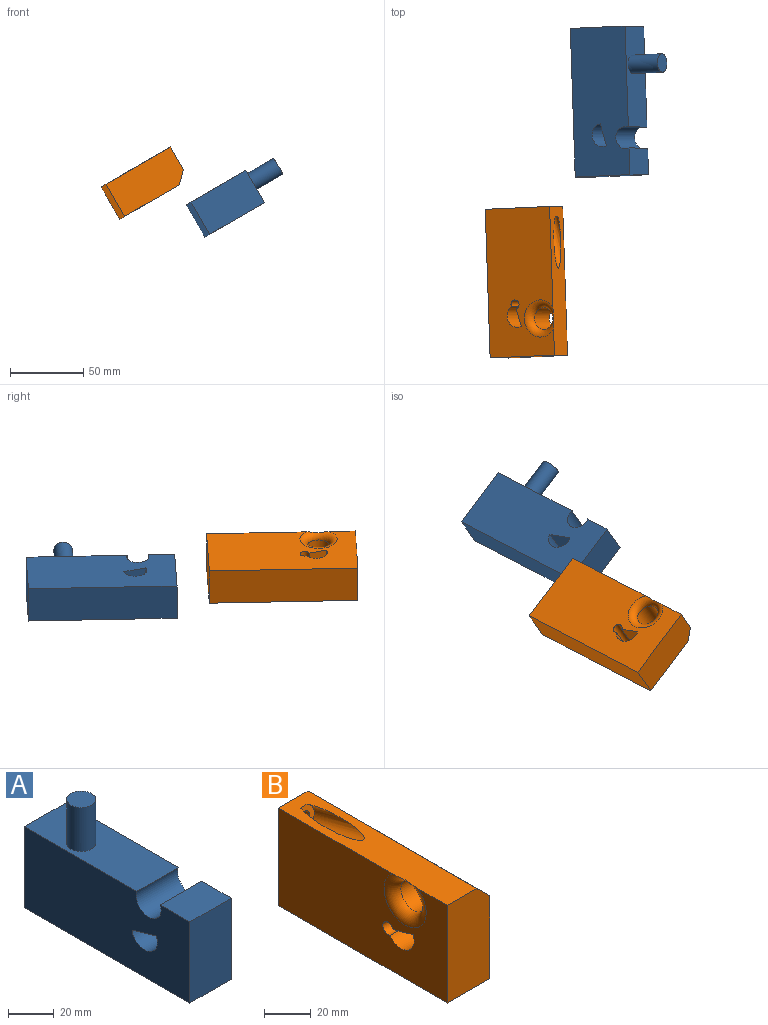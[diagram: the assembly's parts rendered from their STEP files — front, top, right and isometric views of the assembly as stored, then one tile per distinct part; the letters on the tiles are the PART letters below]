
ASSEMBLY  parts=2 mates=1
PART A: 12 faces, bbox 25.4x101.6x66.5 mm
  f0: plane 43.18x25.4mm, normal (0,1,0), area 1096.8mm2, adj f1,f7,f8,f9
  f1: plane 69.02x25.4mm, normal (0,0,1), area 1628.4mm2, adj f0,f2,f8,f9,f10
  f2: cylinder r=7.62mm len=25.4mm, axis (-1,0,0), area 739.6mm2, adj f1,f3,f8,f9
  f3: plane 25.4x18.22mm, normal (0,0,1), area 462.7mm2, adj f2,f4,f8,f9
  f4: plane 43.18x25.4mm, normal (0,-1,0), area 1096.8mm2, adj f3,f7,f8,f9
  f5: cylinder r=7.88mm len=25.4mm, axis (-1,0,0), area 675.4mm2, adj f6,f8,f9
  f6: plane 25.4x15.03mm, normal (0,-0.28,-0.96), area 397.8mm2, adj f5,f8,f9
  f7: plane 101.6x25.4mm, normal (0,0,-1), area 2580.6mm2, adj f0,f4,f8,f9
  f8: plane 101.6x43.18mm, normal (1,0,0), area 4146mm2, adj f0,f1,f2,f3,f4,f5,f6,f7
  f9: plane 101.6x43.18mm, normal (-1,0,0), area 4146mm2, adj f0,f1,f2,f3,f4,f5,f6,f7
  f10: cylinder r=6.3mm len=23.37mm, axis (0,0,-1), area 924.8mm2, adj f1,f11
  f11: plane 12.6x12.6mm, normal (0,0,1), area 124.6mm2, adj f10
PART B: 15 faces, bbox 25.4x102.6x59.7 mm
  f0: plane 101.6x17.78mm, normal (0,0,1), area 1528.8mm2, adj f5,f6,f8,f10,f11,f13,f14
  f1: cylinder r=1.98mm len=9.25mm, axis (0,0.97,-0.26), area 99.4mm2, adj f8,f14
  f2: plane 101.6x43.18mm, normal (1,0,0), area 4122.1mm2, adj f3,f4,f6,f7,f8,f9,f10,f12
  f3: plane 25.4x11.98mm, normal (0,-0.28,-0.96), area 317.2mm2, adj f2,f4,f5,f12
  f4: cylinder r=7.88mm len=25.4mm, axis (1,0,0), area 594.2mm2, adj f2,f3,f5,f12
  f5: plane 101.6x50.8mm, normal (-1,0,0), area 4545.1mm2, adj f0,f3,f4,f6,f7,f8,f11,f12
  f6: plane 50.8x25.4mm, normal (0,-1,0), area 1261.3mm2, adj f0,f2,f5,f7,f10
  f7: plane 101.6x25.4mm, normal (0,0,-1), area 2580.6mm2, adj f2,f5,f6,f8
  f8: plane 50.8x25.4mm, normal (0,1,0), area 1248.5mm2, adj f0,f1,f2,f5,f7,f10
  f9: cylinder r=7.62mm len=20.32mm, axis (1,0,0), area 911mm2, adj f2,f10,f11
  f10: plane 101.6x7.62mm, normal (0.71,0,0.71), area 1019.6mm2, adj f0,f2,f6,f8,f9
  f11: torus R=12.7mm, axis (1,0,0), area 447.4mm2, adj f0,f5,f9
  f12: cylinder r=3.17mm len=25.4mm, axis (1,0,0), area 387.1mm2, adj f2,f3,f4,f5
  f13: cylinder r=4.76mm len=35.73mm, axis (0,0.97,-0.26), area 498.4mm2, adj f0,f14
  f14: plane 9.53x8.89mm, normal (0,-0.97,0.26), area 58.1mm2, adj f0,f1,f13
PLACE A rot(axis=(-0.03,1,0.02),60deg) t=(45.28,27.35,4.81)mm
PLACE B rot(axis=(-0.03,1,0.02),60deg) t=(3.03,-96.22,-10.49)mm
MATE parallel A.f9 <-> B.f5  axis (-0.5,0,0.87) through (57.39,28.61,-24.86)mm
